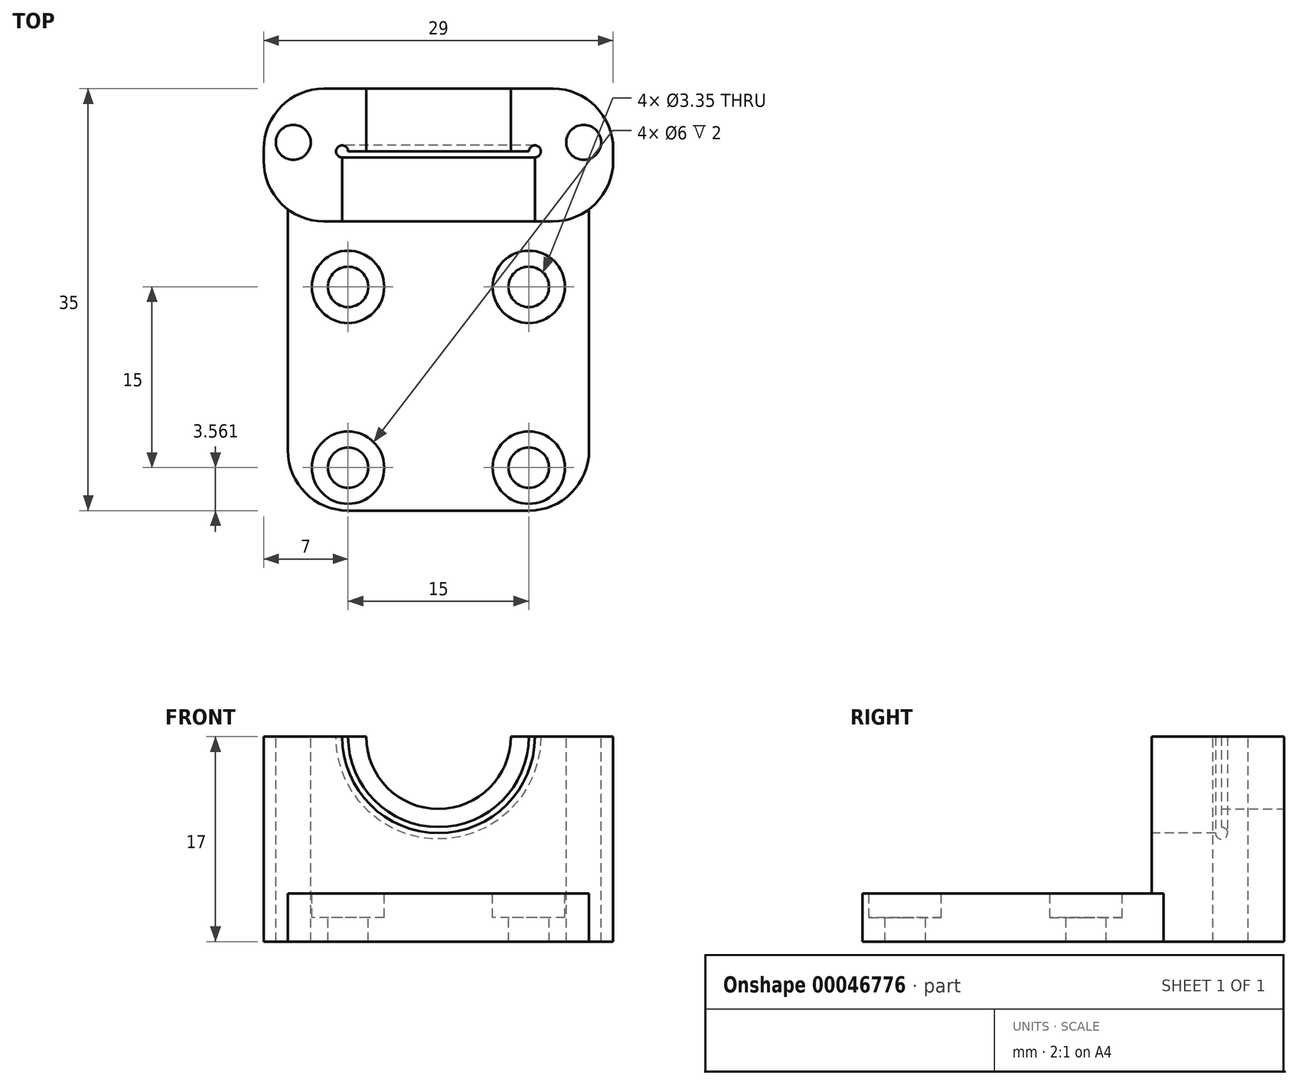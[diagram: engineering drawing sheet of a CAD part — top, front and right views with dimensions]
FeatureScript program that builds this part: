
annotation { "Feature Type Name" : "Feature", "Feature Type Description" : "" }
export const myFeature = defineFeature(function(context is Context, id is Id, definition is map)
    precondition{}
    {
        {
            var Q0;
            Q0=qCreatedBy(makeId("Top.planeOp"),FACE);
            var sketch = newSketch(context, id + "F0", { "sketchPlane" : qUnion([Q0])});
            skLineSegment(sketch, "E0.bottom", {"start": v(0, 0) * mm, "end": v(25, 0) * mm});
            skLineSegment(sketch, "E0.top", {"start": v(0, 35) * mm, "end": v(25, 35) * mm});
            skLineSegment(sketch, "E0.left", {"start": v(0, 0) * mm, "end": v(0, 35) * mm});
            skLineSegment(sketch, "E0.right", {"start": v(25, 0) * mm, "end": v(25, 35) * mm});
            skSolve(sketch);
        }
        {
            var Q0;
            Q0=qSketchRegion(id+"F0",true);
            extrude(context, id + "F1", {"entities" : qUnion([Q0]), "depth" : 4 * mm});
        }
        {
            var Q0;
            Q0=makeQuery(id+"F1.opExtrude","CAP_FACE",FACE,{"disambiguationData":[OSD([sQuery(id+"F0.wireOp",EDGE,"E0.bottom"),sQuery(id+"F0.wireOp",EDGE,"E0.top"),sQuery(id+"F0.wireOp",EDGE,"E0.left"),sQuery(id+"F0.wireOp",EDGE,"E0.right")])],"isStart":false});
            var sketch = newSketch(context, id + "F2", { "sketchPlane" : qUnion([Q0])});
            skCircle(sketch, "E1", {"center": v(5, 18.56) * mm, "radius": 1.68 * mm});
            skCircle(sketch, "E2", {"center": v(20, 18.56) * mm, "radius": 1.68 * mm});
            skCircle(sketch, "E3", {"center": v(5, 3.56) * mm, "radius": 1.68 * mm});
            skCircle(sketch, "E4", {"center": v(20, 3.56) * mm, "radius": 1.68 * mm});
            skLineSegment(sketch, "E5", {"start": v(5, 18.56) * mm, "end": v(0, 18.56) * mm});
            skLineSegment(sketch, "E6", {"start": v(20, 3.56) * mm, "end": v(25, 3.56) * mm});
            skCircle(sketch, "E7", {"center": v(5, 18.56) * mm, "radius": 3 * mm});
            skCircle(sketch, "E8", {"center": v(20, 18.56) * mm, "radius": 3 * mm});
            skCircle(sketch, "E9", {"center": v(5, 3.56) * mm, "radius": 3 * mm});
            skCircle(sketch, "E10", {"center": v(20, 3.56) * mm, "radius": 3 * mm});
            skSolve(sketch);
        }
        {
            var Q0;
            Q0=makeQuery(id+"F2.imprint","IMPRINT",FACE,{"disambiguationData":[TD([[makeQuery(id+"F2.imprint","IMPRINT",EDGE,{"derivedFrom":sQuery(id+"F2.wireOp",EDGE,"E1")}),1.0]])]});
            var Q1;
            Q1=makeQuery(id+"F2.imprint","IMPRINT",FACE,{"disambiguationData":[TD([[makeQuery(id+"F2.imprint","IMPRINT",EDGE,{"derivedFrom":sQuery(id+"F2.wireOp",EDGE,"E2")}),1.0]])]});
            var Q2;
            Q2=makeQuery(id+"F2.imprint","IMPRINT",FACE,{"disambiguationData":[TD([[makeQuery(id+"F2.imprint","IMPRINT",EDGE,{"derivedFrom":sQuery(id+"F2.wireOp",EDGE,"E4")}),1.0]])]});
            var Q3;
            Q3=makeQuery(id+"F2.imprint","IMPRINT",FACE,{"disambiguationData":[TD([[makeQuery(id+"F2.imprint","IMPRINT",EDGE,{"derivedFrom":sQuery(id+"F2.wireOp",EDGE,"E3")}),1.0]])]});
            extrude(context, id + "F3", {"entities" : qUnion([Q0, Q1, Q2, Q3]), "operationType" : NewBodyOperationType.REMOVE, "oppositeDirection" : true, "depth" : 25 * mm});
        }
        {
            var Q0;
            Q0=makeQuery(id+"F1.opExtrude","CAP_FACE",FACE,{"disambiguationData":[OSD([sQuery(id+"F0.wireOp",EDGE,"E0.bottom"),sQuery(id+"F0.wireOp",EDGE,"E0.top"),sQuery(id+"F0.wireOp",EDGE,"E0.left"),sQuery(id+"F0.wireOp",EDGE,"E0.right")])],"isStart":false});
            var sketch = newSketch(context, id + "F4", { "sketchPlane" : qUnion([Q0])});
            skLineSegment(sketch, "E11.bottom", {"start": v(0, 35) * mm, "end": v(25, 35) * mm});
            skLineSegment(sketch, "E11.top", {"start": v(0, 24) * mm, "end": v(25, 24) * mm});
            skLineSegment(sketch, "E11.left", {"start": v(0, 35) * mm, "end": v(0, 24) * mm});
            skLineSegment(sketch, "E11.right", {"start": v(25, 35) * mm, "end": v(25, 24) * mm});
            skSolve(sketch);
        }
        {
            var Q0;
            Q0=qSketchRegion(id+"F4",true);
            extrude(context, id + "F5", {"entities" : qUnion([Q0]), "operationType" : NewBodyOperationType.ADD, "depth" : 13 * mm});
        }
        {
            var Q0;
            Q0=makeQuery(id+"F5.boolean.opBoolean","MERGE",FACE,{"derivedFrom":[makeQuery(id+"F1.opExtrude","SWEPT_FACE",FACE,{"disambiguationData":[OSD([sQuery(id+"F0.wireOp",EDGE,"E0.top")])]}),makeQuery(id+"F5.opExtrude","SWEPT_FACE",FACE,{"disambiguationData":[OSD([sQuery(id+"F4.wireOp",EDGE,"E11.bottom")])]})]});
            var sketch = newSketch(context, id + "F6", { "sketchPlane" : qUnion([Q0])});
            skCircle(sketch, "E12", {"center": v(-12.5, 17) * mm, "radius": 6 * mm});
            skSolve(sketch);
        }
        {
            var Q0;
            {var subQ0=makeQuery(id+"F5.opExtrude","CAP_EDGE",EDGE,{"disambiguationData":[OSD([sQuery(id+"F4.wireOp",EDGE,"E11.bottom")])],"isStart":false});var subQ1=sQuery(id+"F6.wireOp",EDGE,"E12");var subQ3=makeQuery(id+"F6.imprint","INTERSECT",VERTEX,{"disambiguationData":[OD(0.0)],"derivedFrom":[subQ0,subQ1]});Q0=makeQuery(id+"F6.imprint","IMPRINT",FACE,{"disambiguationData":[TD([[makeQuery(id+"F6.imprint","IMPRINT",EDGE,{"disambiguationData":[TD([[subQ3,1.0]])],"derivedFrom":subQ1}),1.0]])]});}
            extrude(context, id + "F7", {"entities" : qUnion([Q0]), "operationType" : NewBodyOperationType.REMOVE, "oppositeDirection" : true, "depth" : 6 * mm});
        }
        {
            var Q0;
            Q0=makeQuery(id+"F5.opExtrude","SWEPT_FACE",FACE,{"disambiguationData":[OSD([sQuery(id+"F4.wireOp",EDGE,"E11.top")])]});
            var sketch = newSketch(context, id + "F8", { "sketchPlane" : qUnion([Q0])});
            skCircle(sketch, "E13", {"center": v(12.5, 17) * mm, "radius": 8 * mm});
            skSolve(sketch);
        }
        {
            var Q0;
            Q0=qSketchRegion(id+"F8",true);
            extrude(context, id + "F9", {"entities" : qUnion([Q0]), "operationType" : NewBodyOperationType.REMOVE, "oppositeDirection" : true, "depth" : 5.8 * mm});
        }
        {
            var Q0;
            Q0=makeQuery(id+"F2.imprint","IMPRINT",FACE,{"disambiguationData":[TD([[makeQuery(id+"F2.imprint","IMPRINT",EDGE,{"derivedFrom":sQuery(id+"F2.wireOp",EDGE,"E1")}),-1.0]])]});
            var Q1;
            Q1=makeQuery(id+"F2.imprint","IMPRINT",FACE,{"disambiguationData":[TD([[makeQuery(id+"F2.imprint","IMPRINT",EDGE,{"derivedFrom":sQuery(id+"F2.wireOp",EDGE,"E2")}),-1.0]])]});
            var Q2;
            Q2=makeQuery(id+"F2.imprint","IMPRINT",FACE,{"disambiguationData":[TD([[makeQuery(id+"F2.imprint","IMPRINT",EDGE,{"derivedFrom":sQuery(id+"F2.wireOp",EDGE,"E4")}),-1.0]])]});
            var Q3;
            Q3=makeQuery(id+"F2.imprint","IMPRINT",FACE,{"disambiguationData":[TD([[makeQuery(id+"F2.imprint","IMPRINT",EDGE,{"derivedFrom":sQuery(id+"F2.wireOp",EDGE,"E3")}),-1.0]])]});
            extrude(context, id + "F10", {"entities" : qUnion([Q0, Q1, Q2, Q3]), "operationType" : NewBodyOperationType.REMOVE, "oppositeDirection" : true, "depth" : 2 * mm});
        }
        {
            var Q0;
            Q0=makeQuery(id+"F1.opExtrude","SWEPT_EDGE",EDGE,{"disambiguationData":[OSD([sQuery(id+"F0.wireOp",EDGE,"E0.bottom"),sQuery(id+"F0.wireOp",EDGE,"E0.left")])]});
            var Q1;
            Q1=makeQuery(id+"F1.opExtrude","SWEPT_EDGE",EDGE,{"disambiguationData":[OSD([sQuery(id+"F0.wireOp",EDGE,"E0.bottom"),sQuery(id+"F0.wireOp",EDGE,"E0.right")])]});
            fillet(context, id + "F11", {"entities" : qUnion([Q0, Q1]), "radius" : 5 * mm, "tangentPropagation" : true, "allowEdgeOverflow" : false});
        }
        {
            var Q0;
            Q0=makeQuery(id+"F5.boolean.opBoolean","MERGE",FACE,{"derivedFrom":[makeQuery(id+"F1.opExtrude","SWEPT_FACE",FACE,{"disambiguationData":[OSD([sQuery(id+"F0.wireOp",EDGE,"E0.left")])]}),makeQuery(id+"F5.opExtrude","SWEPT_FACE",FACE,{"disambiguationData":[OSD([sQuery(id+"F4.wireOp",EDGE,"E11.left")])]})]});
            var sketch = newSketch(context, id + "F12", { "sketchPlane" : qUnion([Q0])});
            skLineSegment(sketch, "E14.bottom", {"start": v(-35, 0) * mm, "end": v(-24, 0) * mm});
            skLineSegment(sketch, "E14.top", {"start": v(-35, 17) * mm, "end": v(-24, 17) * mm});
            skLineSegment(sketch, "E14.left", {"start": v(-35, 0) * mm, "end": v(-35, 17) * mm});
            skLineSegment(sketch, "E14.right", {"start": v(-24, 0) * mm, "end": v(-24, 17) * mm});
            skSolve(sketch);
        }
        {
            var Q0;
            Q0=qSketchRegion(id+"F12",true);
            extrude(context, id + "F13", {"entities" : qUnion([Q0]), "operationType" : NewBodyOperationType.ADD, "depth" : 2 * mm});
        }
        {
            var Q0;
            Q0=makeQuery(id+"F5.boolean.opBoolean","MERGE",FACE,{"derivedFrom":[makeQuery(id+"F1.opExtrude","SWEPT_FACE",FACE,{"disambiguationData":[OSD([sQuery(id+"F0.wireOp",EDGE,"E0.right")])]}),makeQuery(id+"F5.opExtrude","SWEPT_FACE",FACE,{"disambiguationData":[OSD([sQuery(id+"F4.wireOp",EDGE,"E11.right")])]})]});
            var sketch = newSketch(context, id + "F14", { "sketchPlane" : qUnion([Q0])});
            skLineSegment(sketch, "E15.bottom", {"start": v(35, 0) * mm, "end": v(24, 0) * mm});
            skLineSegment(sketch, "E15.top", {"start": v(35, 17) * mm, "end": v(24, 17) * mm});
            skLineSegment(sketch, "E15.left", {"start": v(35, 0) * mm, "end": v(35, 17) * mm});
            skLineSegment(sketch, "E15.right", {"start": v(24, 0) * mm, "end": v(24, 17) * mm});
            skSolve(sketch);
        }
        {
            var Q0;
            Q0=qSketchRegion(id+"F14",true);
            extrude(context, id + "F15", {"entities" : qUnion([Q0]), "operationType" : NewBodyOperationType.ADD, "depth" : 2 * mm});
        }
        {
            var Q0;
            {var subQ0=sQuery(id+"F4.wireOp",EDGE,"E11.bottom");var subQ1=sQuery(id+"F4.wireOp",EDGE,"E11.top");var subQ2=sQuery(id+"F4.wireOp",EDGE,"E11.left");Q0=makeQuery(id+"F9.boolean.opBoolean","SPLIT",FACE,{"disambiguationData":[TD([makeQuery(id+"F1.opExtrude","SWEPT_FACE",FACE,{"disambiguationData":[OSD([sQuery(id+"F0.wireOp",EDGE,"E0.left")])]})])],"derivedFrom":makeQuery(id+"F5.opExtrude","CAP_FACE",FACE,{"disambiguationData":[OSD([subQ0,subQ1,subQ2,sQuery(id+"F4.wireOp",EDGE,"E11.right")])],"isStart":false})});}
            var sketch = newSketch(context, id + "F16", { "sketchPlane" : qUnion([Q0])});
            skCircle(sketch, "E16", {"center": v(0.45, 30.55) * mm, "radius": 1.45 * mm});
            skCircle(sketch, "E17", {"center": v(24.55, 30.55) * mm, "radius": 1.45 * mm});
            skSolve(sketch);
        }
        {
            var Q0;
            Q0=qSketchRegion(id+"F16",true);
            extrude(context, id + "F17", {"entities" : qUnion([Q0]), "operationType" : NewBodyOperationType.REMOVE, "oppositeDirection" : true, "depth" : 25 * mm});
        }
        {
            var Q0;
            Q0=makeQuery(id+"F13.opExtrude","CAP_EDGE",EDGE,{"disambiguationData":[OSD([sQuery(id+"F12.wireOp",EDGE,"E14.right")])],"isStart":false});
            var Q1;
            Q1=makeQuery(id+"F13.opExtrude","CAP_EDGE",EDGE,{"disambiguationData":[OSD([sQuery(id+"F12.wireOp",EDGE,"E14.left")])],"isStart":false});
            var Q2;
            Q2=makeQuery(id+"F15.opExtrude","CAP_EDGE",EDGE,{"disambiguationData":[OSD([sQuery(id+"F14.wireOp",EDGE,"E15.left")])],"isStart":false});
            var Q3;
            Q3=makeQuery(id+"F15.opExtrude","CAP_EDGE",EDGE,{"disambiguationData":[OSD([sQuery(id+"F14.wireOp",EDGE,"E15.right")])],"isStart":false});
            fillet(context, id + "F18", {"entities" : qUnion([Q0, Q1, Q2, Q3]), "radius" : 5 * mm, "tangentPropagation" : true, "allowEdgeOverflow" : false});
        }
        {
            var Q0;
            {var subQ0=sQuery(id+"F4.wireOp",EDGE,"E11.bottom");var subQ1=sQuery(id+"F4.wireOp",EDGE,"E11.top");var subQ2=sQuery(id+"F4.wireOp",EDGE,"E11.right");Q0=makeQuery(id+"F15.boolean.opBoolean","MERGE",FACE,{"derivedFrom":[makeQuery(id+"F9.boolean.opBoolean","SPLIT",FACE,{"disambiguationData":[TD([makeQuery(id+"F1.opExtrude","SWEPT_FACE",FACE,{"disambiguationData":[OSD([sQuery(id+"F0.wireOp",EDGE,"E0.right")])]})])],"derivedFrom":makeQuery(id+"F5.opExtrude","CAP_FACE",FACE,{"disambiguationData":[OSD([subQ0,subQ1,sQuery(id+"F4.wireOp",EDGE,"E11.left"),subQ2])],"isStart":false})}),makeQuery(id+"F15.opExtrude","SWEPT_FACE",FACE,{"disambiguationData":[OSD([sQuery(id+"F14.wireOp",EDGE,"E15.top")])]})]});}
            var sketch = newSketch(context, id + "F19", { "sketchPlane" : qUnion([Q0])});
            skCircle(sketch, "E18", {"center": v(20.5, 29.8) * mm, "radius": 0.5 * mm});
            skSolve(sketch);
        }
        {
            var Q0;
            {var subQ0=makeQuery(id+"F5.opExtrude","CAP_FACE",FACE,{"disambiguationData":[OSD([sQuery(id+"F4.wireOp",EDGE,"E11.bottom"),sQuery(id+"F4.wireOp",EDGE,"E11.top"),sQuery(id+"F4.wireOp",EDGE,"E11.left"),sQuery(id+"F4.wireOp",EDGE,"E11.right")])],"isStart":false});var subQ1=sQuery(id+"F8.wireOp",EDGE,"E13");var subQ3=sQuery(id+"F19.wireOp",EDGE,"E18");var subQ5=makeQuery(id+"F9.boolean.opBoolean","INTERSECT",EDGE,{"disambiguationData":[OD(1.0)],"derivedFrom":[subQ0,makeQuery(id+"F9.opExtrude","SWEPT_FACE",FACE,{"disambiguationData":[OSD([subQ1])]})]});var subQ7=makeQuery(id+"F19.imprint","INTERSECT",VERTEX,{"derivedFrom":[subQ5,subQ3]});Q0=makeQuery(id+"F19.imprint","IMPRINT",FACE,{"disambiguationData":[TD([[makeQuery(id+"F19.imprint","IMPRINT",EDGE,{"disambiguationData":[TD([[subQ7,-1.0]])],"derivedFrom":subQ3}),1.0]])]});}
            var Q1;
            Q1=makeQuery(id+"F7.boolean.opBoolean","COPY",FACE,{"derivedFrom":makeQuery(id+"F7.opExtrude","SWEPT_FACE",FACE,{"disambiguationData":[OSD([sQuery(id+"F6.wireOp",EDGE,"E12")])]})});
            revolve(context, id + "F20", {"operationType" : NewBodyOperationType.REMOVE, "entities" : qUnion([Q0]), "axis" : qUnion([Q1]), "revolveType" : RevolveType.FULL, "oppositeDirection" : true});
        }
    });
